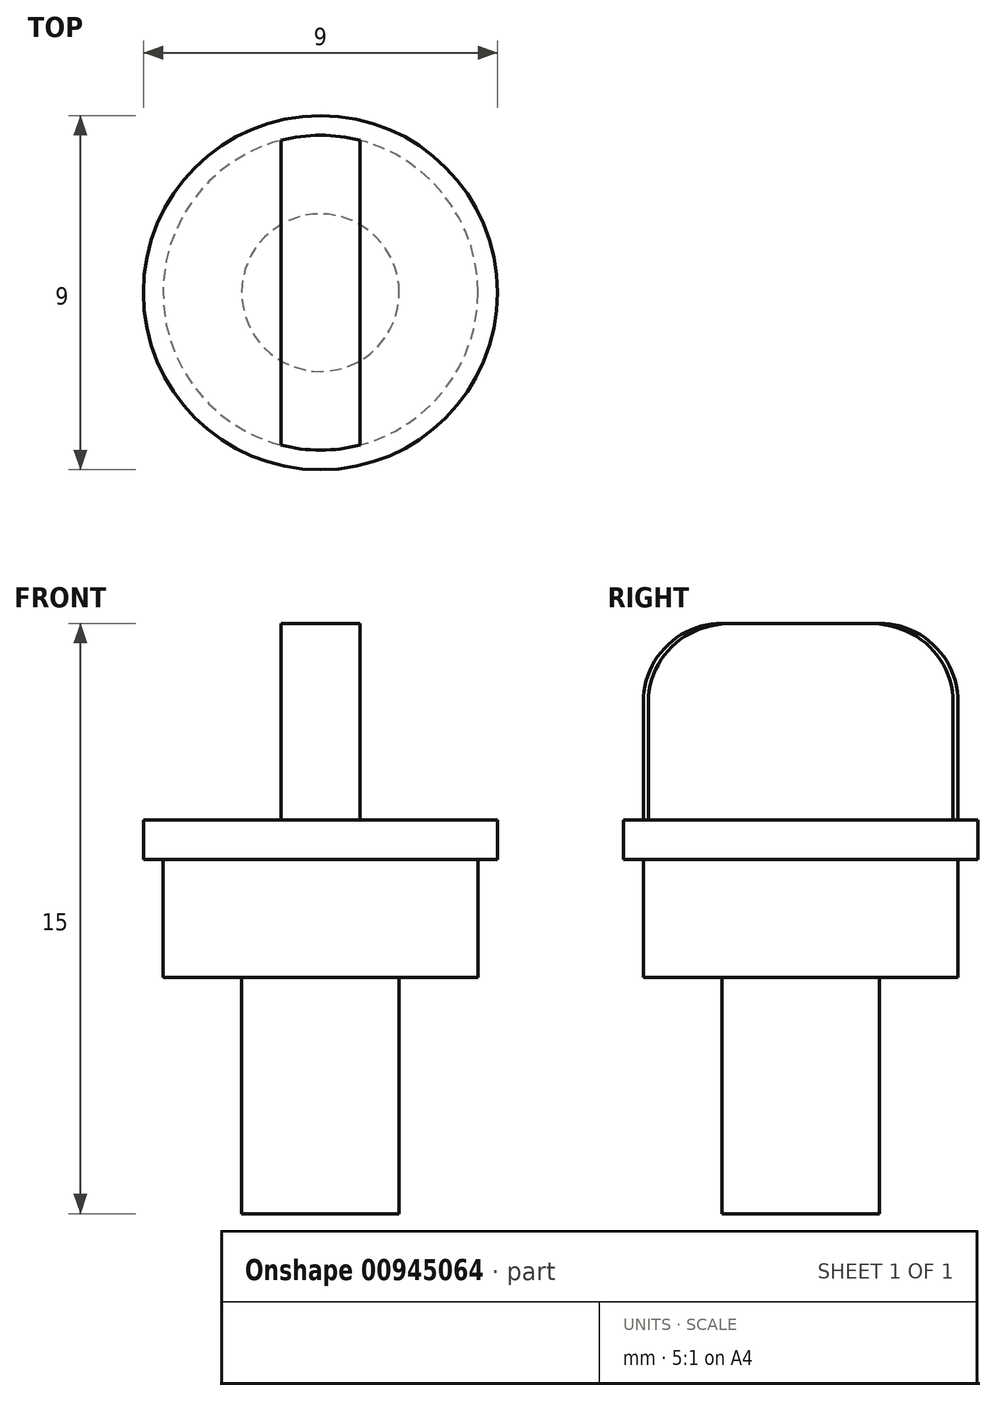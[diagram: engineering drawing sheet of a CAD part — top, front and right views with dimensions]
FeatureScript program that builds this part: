
annotation { "Feature Type Name" : "Feature", "Feature Type Description" : "" }
export const myFeature = defineFeature(function(context is Context, id is Id, definition is map)
    precondition{}
    {
        {
            var Q0;
            Q0=qCreatedBy(makeId("Front.planeOp"),FACE);
            var sketch = newSketch(context, id + "F0", { "sketchPlane" : qUnion([Q0])});
            skLineSegment(sketch, "E0", {"start": v(0, 0) * mm, "end": v(2, 0) * mm});
            skLineSegment(sketch, "E1", {"start": v(2, 0) * mm, "end": v(2, 6) * mm});
            skLineSegment(sketch, "E2", {"start": v(2, 6) * mm, "end": v(4, 6) * mm});
            skLineSegment(sketch, "E3", {"start": v(4, 6) * mm, "end": v(4, 9) * mm});
            skLineSegment(sketch, "E4", {"start": v(4, 9) * mm, "end": v(4.5, 9) * mm});
            skLineSegment(sketch, "E5", {"start": v(4.5, 9) * mm, "end": v(4.5, 10) * mm});
            skLineSegment(sketch, "E6", {"start": v(4.5, 10) * mm, "end": v(4, 10) * mm});
            skLineSegment(sketch, "E7", {"start": v(4, 10) * mm, "end": v(4, 15) * mm});
            skLineSegment(sketch, "E8", {"start": v(4, 15) * mm, "end": v(0, 15) * mm});
            skLineSegment(sketch, "E9", {"start": v(0, 15) * mm, "end": v(0, 0) * mm});
            skSolve(sketch);
        }
        {
            var Q0;
            Q0=makeQuery(id+"F0.imprint","IMPRINT",FACE,{"disambiguationData":[TD([[makeQuery(id+"F0.imprint","IMPRINT",EDGE,{"derivedFrom":sQuery(id+"F0.wireOp",EDGE,"E0")}),1.0]])]});
            var Q1;
            Q1=sQuery(id+"F0.wireOp",EDGE,"E9");
            revolve(context, id + "F1", {"surfaceOperationType" : NewSurfaceOperationType.NEW, "entities" : qUnion([Q0]), "axis" : qUnion([Q1]), "revolveType" : RevolveType.FULL});
        }
        {
            var Q0;
            Q0=makeQuery(id+"F1.opRevolve","SWEPT_FACE",FACE,{"disambiguationData":[OSD([sQuery(id+"F0.wireOp",EDGE,"E8")])]});
            var sketch = newSketch(context, id + "F2", { "sketchPlane" : qUnion([Q0])});
            skLineSegment(sketch, "E10", {"start": v(-1, 3.87) * mm, "end": v(-1, -3.87) * mm});
            skLineSegment(sketch, "E11", {"start": v(1, 3.87) * mm, "end": v(1, -3.87) * mm});
            skSolve(sketch);
        }
        {
            var Q0;
            {var subQ0=sQuery(id+"F2.wireOp",EDGE,"E10");Q0=makeQuery(id+"F2.imprint","IMPRINT",FACE,{"disambiguationData":[TD([[makeQuery(id+"F2.imprint","IMPRINT",EDGE,{"derivedFrom":subQ0}),-1.0]])]});}
            var Q1;
            {var subQ0=sQuery(id+"F2.wireOp",EDGE,"E11");Q1=makeQuery(id+"F2.imprint","IMPRINT",FACE,{"disambiguationData":[TD([[makeQuery(id+"F2.imprint","IMPRINT",EDGE,{"derivedFrom":subQ0}),1.0]])]});}
            var Q2;
            Q2=makeQuery(id+"F1.opRevolve","SWEPT_FACE",FACE,{"disambiguationData":[OSD([sQuery(id+"F0.wireOp",EDGE,"E6")])]});
            extrude(context, id + "F3", {"entities" : qUnion([Q0, Q1]), "operationType" : NewBodyOperationType.REMOVE, "endBound" : BoundingType.UP_TO_SURFACE, "oppositeDirection" : true, "depth" : 25 * mm, "endBoundEntityFace" : qUnion([Q2]), "offsetDistance" : 25 * mm});
        }
        {
            var Q0;
            Q0=makeQuery(id+"F3.boolean.opBoolean","SPLIT",EDGE,{"disambiguationData":[OD(1.0)],"derivedFrom":makeQuery(id+"F1.opRevolve","SWEPT_EDGE",EDGE,{"disambiguationData":[OSD([sQuery(id+"F0.wireOp",EDGE,"E7"),sQuery(id+"F0.wireOp",EDGE,"E8")])]})});
            var Q1;
            Q1=makeQuery(id+"F3.boolean.opBoolean","SPLIT",EDGE,{"disambiguationData":[OD(0.0)],"derivedFrom":makeQuery(id+"F1.opRevolve","SWEPT_EDGE",EDGE,{"disambiguationData":[OSD([sQuery(id+"F0.wireOp",EDGE,"E7"),sQuery(id+"F0.wireOp",EDGE,"E8")])]})});
            fillet(context, id + "F4", {"entities" : qUnion([Q0, Q1]), "radius" : 2 * mm, "tangentPropagation" : true, "allowEdgeOverflow" : false});
        }
    });
